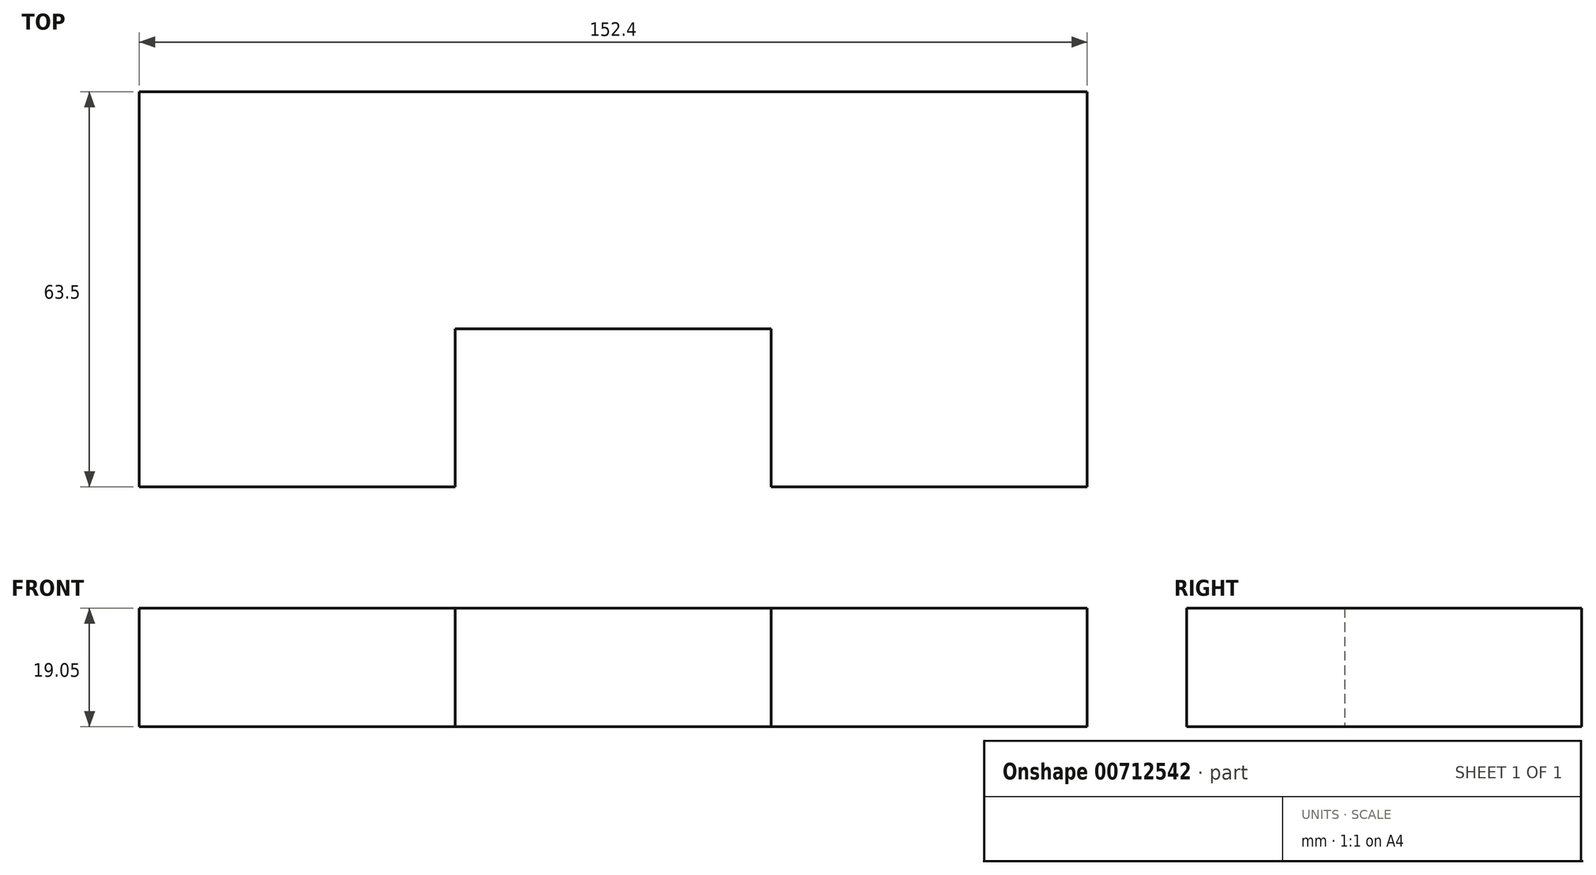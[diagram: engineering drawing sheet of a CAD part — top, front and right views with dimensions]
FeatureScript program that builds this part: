
annotation { "Feature Type Name" : "Feature", "Feature Type Description" : "" }
export const myFeature = defineFeature(function(context is Context, id is Id, definition is map)
    precondition{}
    {
        {
            var Q0;
            Q0=qCreatedBy(makeId("Top.planeOp"),FACE);
            var sketch = newSketch(context, id + "F0", { "sketchPlane" : qUnion([Q0])});
            skLineSegment(sketch, "E0.bottom", {"start": v(76.2, -31.75) * mm, "end": v(-76.2, -31.75) * mm});
            skLineSegment(sketch, "E0.top", {"start": v(76.2, 31.75) * mm, "end": v(-76.2, 31.75) * mm});
            skLineSegment(sketch, "E0.left", {"start": v(76.2, -31.75) * mm, "end": v(76.2, 31.75) * mm});
            skLineSegment(sketch, "E0.right", {"start": v(-76.2, -31.75) * mm, "end": v(-76.2, 31.75) * mm});
            skPoint(sketch, "E0.middle", {"position": v(0, 0) * mm});
            skLineSegment(sketch, "E1.bottom", {"start": v(25.4, -57.15) * mm, "end": v(-25.4, -57.15) * mm});
            skLineSegment(sketch, "E1.top", {"start": v(25.4, -6.35) * mm, "end": v(-25.4, -6.35) * mm});
            skLineSegment(sketch, "E1.left", {"start": v(25.4, -57.15) * mm, "end": v(25.4, -6.35) * mm});
            skLineSegment(sketch, "E1.right", {"start": v(-25.4, -57.15) * mm, "end": v(-25.4, -6.35) * mm});
            skPoint(sketch, "E1.middle", {"position": v(0, -31.75) * mm});
            skSolve(sketch);
        }
        {
            var Q0;
            Q0=makeQuery(id+"F0.imprint","IMPRINT",FACE,{"disambiguationData":[TD([[makeQuery(id+"F0.imprint","IMPRINT",EDGE,{"derivedFrom":sQuery(id+"F0.wireOp",EDGE,"E0.top")}),1.0]])]});
            extrude(context, id + "F1", {"entities" : qUnion([Q0]), "depth" : 19.05 * mm, "offsetDistance" : 25.4 * mm});
        }
    });
